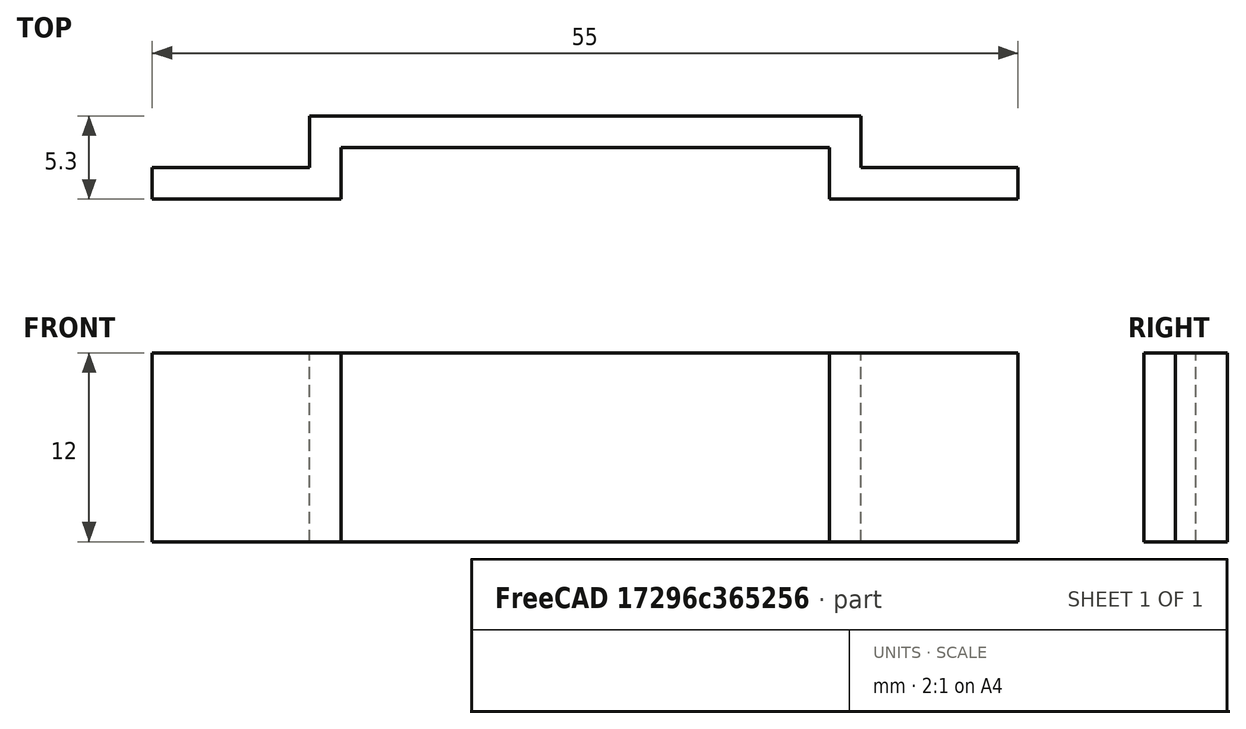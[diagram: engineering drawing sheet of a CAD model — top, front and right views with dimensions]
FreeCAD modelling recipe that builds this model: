
FCSTD DOCUMENT  (FreeCAD 0.16R6698 (Git))
Label: steval-holder
License: All rights reserved
LicenseURL: http://en.wikipedia.org/wiki/All_rights_reserved
objects: Sketcher::SketchObject×1, Part::Extrusion×1
note: 2 computed .brp shape members not serialized (recipe doc carries the construction recipe); baked Part::Feature solids carry a one-line shape summary decoded from their .brp

FEATURE [Sketcher::SketchObject] Sketch
  sketch-geometry (12):
    g0: LineSegment StartX=-27.5 StartY=0 StartZ=0 EndX=-15.5 EndY=0 EndZ=0
    g1: LineSegment StartX=-15.5 StartY=3.3 StartZ=0 EndX=15.5 EndY=3.3 EndZ=0
    g2: LineSegment StartX=15.5 StartY=3.3 StartZ=0 EndX=15.5 EndY=0 EndZ=0
    g3: LineSegment StartX=15.5 StartY=0 StartZ=0 EndX=27.5 EndY=0 EndZ=0
    g4: LineSegment StartX=27.5 StartY=0 StartZ=0 EndX=27.5 EndY=2 EndZ=0
    g5: LineSegment StartX=27.5 StartY=2 StartZ=0 EndX=17.5 EndY=2 EndZ=0
    g6: LineSegment StartX=17.5 StartY=2 StartZ=0 EndX=17.5 EndY=5.3 EndZ=0
    g7: LineSegment StartX=17.5 StartY=5.3 StartZ=0 EndX=-17.5 EndY=5.3 EndZ=0
    g8: LineSegment StartX=-17.5 StartY=5.3 StartZ=0 EndX=-17.5 EndY=2 EndZ=0
    g9: LineSegment StartX=-17.5 StartY=2 StartZ=0 EndX=-27.5 EndY=2 EndZ=0
    g10: LineSegment StartX=-27.5 StartY=2 StartZ=0 EndX=-27.5 EndY=0 EndZ=0
    g11: LineSegment StartX=-15.5 StartY=0 StartZ=0 EndX=-15.5 EndY=3.3 EndZ=0
  constraints (36):
    c: PointOnObject(g0,g-1)
    c: Horizontal(g1)
    c: Coincident(g1,g2)
    c: PointOnObject(g2,g-1)
    c: Vertical(g2)
    c: Coincident(g2,g3)
    c: Horizontal(g3)
    c: Coincident(g3,g4)
    c: Vertical(g4)
    c: Coincident(g4,g5)
    c: Coincident(g5,g6)
    c: Vertical(g6)
    c: Coincident(g6,g7)
    c: Horizontal(g7)
    c: Coincident(g7,g8)
    c: Vertical(g8)
    c: Coincident(g8,g9)
    c: Horizontal(g9)
    c: Coincident(g9,g10)
    c: Coincident(g10,g0)
    c: Vertical(g10)
    c: Horizontal(g5)
    c: Horizontal(g0)
    c: Equal(g3,g0)
    c: Equal(g9,g5)
    c: Equal(g10,g4)
    c: DistanceX(g5,g5) = 10
    c: DistanceX(g1,g1) = 31
    c: DistanceX(g7,g7) = 35
    c: DistanceY(g4,g4) = 2
    c: Coincident(g11,g0)
    c: Vertical(g11)
    c: Coincident(g11,g1)
    c: DistanceY(g11,g11) = 3.3
    c: Symmetric(g1,g1,g-2)
    c: DistanceY(g1,g7) = 2
FEATURE [Part::Extrusion] Extrude
  Base = -> Sketch
  Dir = (0,0,12)
  Solid = true
